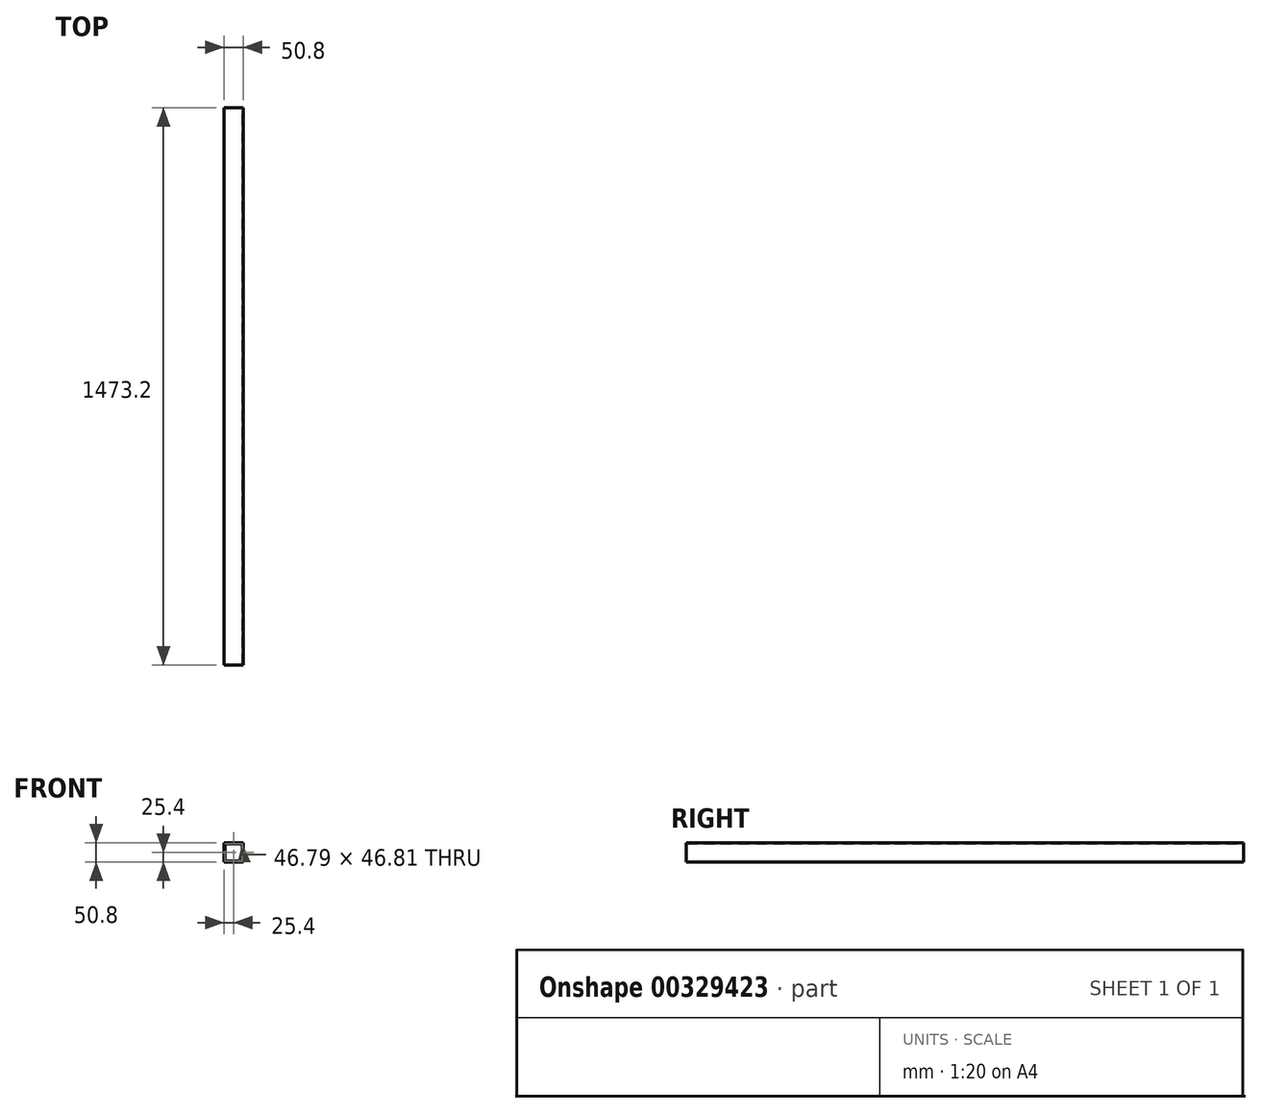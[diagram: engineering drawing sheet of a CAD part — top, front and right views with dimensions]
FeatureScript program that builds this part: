
annotation { "Feature Type Name" : "Feature", "Feature Type Description" : "" }
export const myFeature = defineFeature(function(context is Context, id is Id, definition is map)
    precondition{}
    {
        {
            var Q0;
            Q0=qCreatedBy(makeId("Front.planeOp"),FACE);
            var sketch = newSketch(context, id + "F0", { "sketchPlane" : qUnion([Q0])});
            skLineSegment(sketch, "E0.bottom", {"start": v(25.4, -25.4) * mm, "end": v(-25.4, -25.4) * mm});
            skLineSegment(sketch, "E0.top", {"start": v(25.4, 25.4) * mm, "end": v(-25.4, 25.4) * mm});
            skLineSegment(sketch, "E0.left", {"start": v(25.4, -25.4) * mm, "end": v(25.4, 25.4) * mm});
            skLineSegment(sketch, "E0.right", {"start": v(-25.4, -25.4) * mm, "end": v(-25.4, 25.4) * mm});
            skPoint(sketch, "E0.middle", {"position": v(0, 0) * mm});
            skLineSegment(sketch, "E1.bottom", {"start": v(23.4, -23.4) * mm, "end": v(-23.4, -23.4) * mm});
            skLineSegment(sketch, "E1.top", {"start": v(23.4, 23.4) * mm, "end": v(-23.4, 23.4) * mm});
            skLineSegment(sketch, "E1.left", {"start": v(23.4, -23.4) * mm, "end": v(23.4, 23.4) * mm});
            skLineSegment(sketch, "E1.right", {"start": v(-23.4, -23.4) * mm, "end": v(-23.4, 23.4) * mm});
            skSolve(sketch);
        }
        {
            var Q0;
            Q0=qSketchRegion(id+"F0",true);
            extrude(context, id + "F1", {"entities" : qUnion([Q0]), "depth" : 1473.2 * mm});
        }
    });
